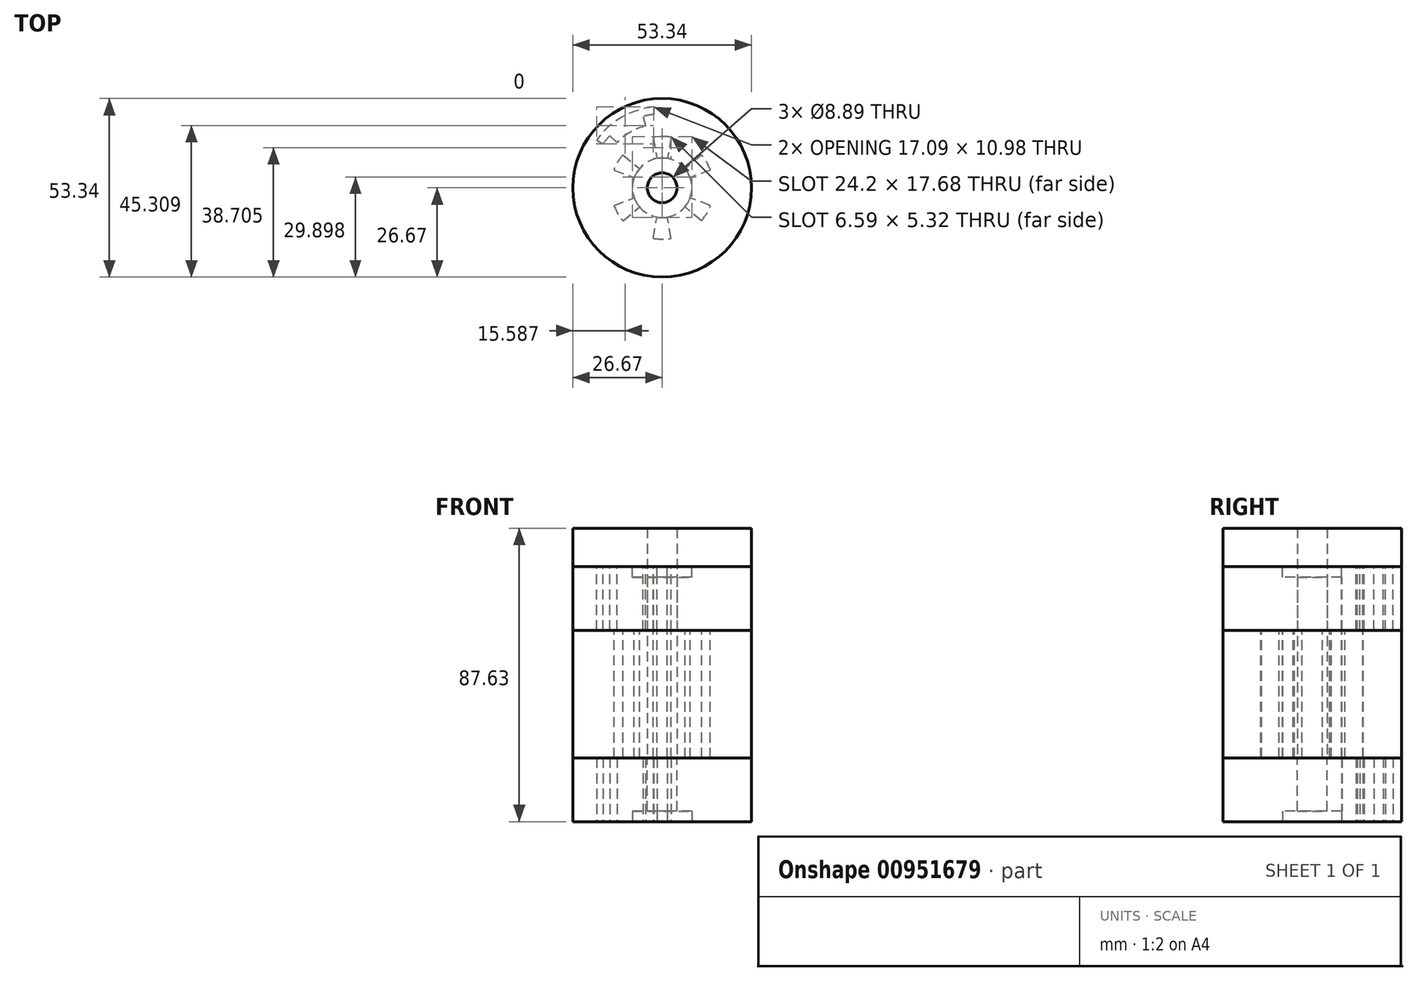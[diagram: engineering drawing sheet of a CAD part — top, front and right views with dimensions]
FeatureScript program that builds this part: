
annotation { "Feature Type Name" : "Feature", "Feature Type Description" : "" }
export const myFeature = defineFeature(function(context is Context, id is Id, definition is map)
    precondition{}
    {
        {
            var Q0;
            Q0=qCreatedBy(makeId("Top.planeOp"),FACE);
            var sketch = newSketch(context, id + "F0", { "sketchPlane" : qUnion([Q0])});
            skCircle(sketch, "E0", {"center": v(0, 0) * mm, "radius": 26.67 * mm});
            skCircle(sketch, "E1", {"center": v(0, 0) * mm, "radius": 4.45 * mm});
            skSolve(sketch);
        }
        {
            var Q0;
            Q0=qSketchRegion(id+"F0",true);
            extrude(context, id + "F1", {"entities" : qUnion([Q0]), "depth" : 19.05 * mm});
        }
        {
            var Q0;
            Q0=makeQuery(id+"F1.opExtrude","CAP_FACE",FACE,{"disambiguationData":[OSD([sQuery(id+"F0.wireOp",EDGE,"E0"),sQuery(id+"F0.wireOp",EDGE,"E1")])],"isStart":false});
            var sketch = newSketch(context, id + "F2", { "sketchPlane" : qUnion([Q0])});
            skCircle(sketch, "E2", {"center": v(0, 0) * mm, "radius": 24.26 * mm, "construction": true});
            skCircle(sketch, "E3", {"center": v(0, 0) * mm, "radius": 22.05 * mm, "construction": true});
            skCircle(sketch, "E4", {"center": v(0, 0) * mm, "radius": 19.11 * mm, "construction": true});
            skLineSegment(sketch, "E5", {"start": v(0, 0) * mm, "end": v(-23.1, 13.34) * mm, "construction": true});
            skLineSegment(sketch, "E6", {"start": v(-2.54, 24.13) * mm, "end": v(-2.54, 21.9) * mm});
            skLineSegment(sketch, "E7", {"start": v(-19.63, 14.26) * mm, "end": v(-17.7, 13.15) * mm});
            skArc(sketch, "E8", {"start": v(-2.54, 24.13) * mm, "mid": v(-12.13, 21.01) * mm, "end": v(-19.63, 14.26) * mm});
            skLineSegment(sketch, "E9", {"start": v(0, 0) * mm, "end": v(-15.59, 15.59) * mm, "construction": true});
            skLineSegment(sketch, "E10", {"start": v(0, 0) * mm, "end": v(-5.7, 21.3) * mm, "construction": true});
            skLineSegment(sketch, "E11", {"start": v(-15.59, 15.59) * mm, "end": v(-13.51, 13.51) * mm});
            skLineSegment(sketch, "E12", {"start": v(-5.7, 21.3) * mm, "end": v(-4.95, 18.46) * mm});
            skArc(sketch, "E13", {"start": v(-17.7, 13.15) * mm, "mid": v(-16.69, 14.4) * mm, "end": v(-15.59, 15.59) * mm});
            skArc(sketch, "E14", {"start": v(-2.54, 21.9) * mm, "mid": v(-4.13, 21.65) * mm, "end": v(-5.7, 21.3) * mm});
            skArc(sketch, "E15", {"start": v(-13.51, 13.51) * mm, "mid": v(-9.56, 16.55) * mm, "end": v(-4.95, 18.46) * mm});
            skSolve(sketch);
        }
        {
            var Q0;
            Q0=qSketchRegion(id+"F2",true);
            extrude(context, id + "F3", {"entities" : qUnion([Q0]), "operationType" : NewBodyOperationType.REMOVE, "endBound" : BoundingType.THROUGH_ALL, "oppositeDirection" : true, "depth" : 25.4 * mm});
        }
        {
            var Q0;
            Q0=qCreatedBy(makeId("Right.planeOp"),FACE);
            var sketch = newSketch(context, id + "F4", { "sketchPlane" : qUnion([Q0])});
            skLineSegment(sketch, "E16", {"start": v(0, 63.62) * mm, "end": v(0, 1.5) * mm});
            skSolve(sketch);
        }
        {
            var Q0;
            Q0=makeQuery(id+"F1.opExtrude","CAP_FACE",FACE,{"disambiguationData":[OSD([sQuery(id+"F0.wireOp",EDGE,"E0"),sQuery(id+"F0.wireOp",EDGE,"E1")])],"isStart":false});
            var sketch = newSketch(context, id + "F5", { "sketchPlane" : qUnion([Q0])});
            skCircle(sketch, "E17", {"center": v(0, 0) * mm, "radius": 15.33 * mm, "construction": true});
            skCircle(sketch, "E18", {"center": v(0, 0) * mm, "radius": 8.87 * mm, "construction": true});
            skLineSegment(sketch, "E19", {"start": v(0, 0) * mm, "end": v(-2.66, 15.1) * mm, "construction": true});
            skLineSegment(sketch, "E20", {"start": v(0, 0) * mm, "end": v(2.66, 15.1) * mm, "construction": true});
            skLineSegment(sketch, "E21", {"start": v(-2.66, 15.1) * mm, "end": v(-1.54, 8.74) * mm});
            skLineSegment(sketch, "E22", {"start": v(2.66, 15.1) * mm, "end": v(1.54, 8.74) * mm});
            skArc(sketch, "E23", {"start": v(-1.54, 8.74) * mm, "mid": v(0, 8.87) * mm, "end": v(1.54, 8.74) * mm});
            skArc(sketch, "E24", {"start": v(-2.66, 15.1) * mm, "mid": v(0, 15.33) * mm, "end": v(2.66, 15.1) * mm});
            skSolve(sketch);
        }
        {
            var Q0;
            Q0=qSketchRegion(id+"F5",true);
            extrude(context, id + "F6", {"entities" : qUnion([Q0]), "operationType" : NewBodyOperationType.REMOVE, "endBound" : BoundingType.THROUGH_ALL, "oppositeDirection" : true, "depth" : 25.4 * mm});
        }
        {
            var Q0;
            Q0=makeQuery(id+"F1.opExtrude","CAP_FACE",FACE,{"disambiguationData":[OSD([sQuery(id+"F0.wireOp",EDGE,"E0"),sQuery(id+"F0.wireOp",EDGE,"E1")])],"isStart":false});
            var sketch = newSketch(context, id + "F7", { "sketchPlane" : qUnion([Q0])});
            skCircle(sketch, "E25", {"center": v(0, 0) * mm, "radius": 8.87 * mm});
            skSolve(sketch);
        }
        {
            var Q0;
            Q0=qSketchRegion(id+"F7",true);
            extrude(context, id + "F8", {"entities" : qUnion([Q0]), "operationType" : NewBodyOperationType.REMOVE, "oppositeDirection" : true, "depth" : 3.17 * mm});
        }
        {
            var Q0;
            Q0=makeQuery(id+"F1.opExtrude","CAP_FACE",FACE,{"disambiguationData":[OSD([sQuery(id+"F0.wireOp",EDGE,"E0"),sQuery(id+"F0.wireOp",EDGE,"E1")])],"isStart":true});
            var sketch = newSketch(context, id + "F9", { "sketchPlane" : qUnion([Q0])});
            skArc(sketch, "E26", {"start": v(-2.66, -15.1) * mm, "mid": v(0, -15.33) * mm, "end": v(2.66, -15.1) * mm});
            skArc(sketch, "E27", {"start": v(-1.54, -8.74) * mm, "mid": v(0, -8.87) * mm, "end": v(1.54, -8.74) * mm});
            skLineSegment(sketch, "E28", {"start": v(2.66, -15.1) * mm, "end": v(1.54, -8.74) * mm});
            skLineSegment(sketch, "E29", {"start": v(-2.66, -15.1) * mm, "end": v(-1.54, -8.74) * mm});
            skSolve(sketch);
        }
        {
            var Q0;
            Q0=qSketchRegion(id+"F9",true);
            extrude(context, id + "F10", {"entities" : qUnion([Q0]), "depth" : 38.1 * mm});
        }
        {
            var Q0;
            Q0=makeQuery(id+"F10.opExtrude","SWEPT_BODY",BODY,{"disambiguationData":[OSD([sQuery(id+"F9.wireOp",EDGE,"E26"),sQuery(id+"F9.wireOp",EDGE,"E27"),sQuery(id+"F9.wireOp",EDGE,"E28"),sQuery(id+"F9.wireOp",EDGE,"E29")])]});
            var Q1;
            Q1=sQuery(id+"F4.wireOp",EDGE,"E16");
            circularPattern(context, id + "F11", {"entities" : qUnion([Q0]), "axis" : qUnion([Q1]), "angle" : 360 * degree, "instanceCount" : 6, "equalSpace" : true});
        }
        {
            var Q0;
            Q0=qCreatedBy(makeId("Top.planeOp"),FACE);
            cPlane(context, id + "F12", {"entities" : qUnion([Q0]), "cplaneType" : CPlaneType.OFFSET, "offset" : 19.05 * mm, "oppositeDirection" : true, "width" : 152.4 * mm, "height" : 152.4 * mm});
        }
        {
            var Q0;
            Q0=makeQuery(id+"F1.opExtrude","SWEPT_BODY",BODY,{"disambiguationData":[OSD([sQuery(id+"F0.wireOp",EDGE,"E0"),sQuery(id+"F0.wireOp",EDGE,"E1")])]});
            var Q1;
            Q1=qCreatedBy(id+"F12.planeOp",FACE);
            mirror(context, id + "F13", {"entities" : qUnion([Q0]), "mirrorPlane" : qUnion([Q1])});
        }
        {
            var Q0;
            Q0=makeQuery(id+"F13.opPattern","COPY",FACE,{"derivedFrom":makeQuery(id+"F1.opExtrude","CAP_FACE",FACE,{"disambiguationData":[OSD([sQuery(id+"F0.wireOp",EDGE,"E0"),sQuery(id+"F0.wireOp",EDGE,"E1")])],"isStart":true}),"instanceName":"1"});
            var sketch = newSketch(context, id + "F14", { "sketchPlane" : qUnion([Q0])});
            skCircle(sketch, "E30", {"center": v(0, 0) * mm, "radius": 26.67 * mm});
            skCircle(sketch, "E31", {"center": v(0, 0) * mm, "radius": 4.45 * mm});
            skSolve(sketch);
        }
        {
            var Q0;
            Q0 = qSketchRegion(id + "F14", true);
            extrude(context, id + "F15", {"entities" : qUnion([Q0]), "depth" : 68.58 * mm, "offsetDistance" : 25.4 * mm});
        }
    });
